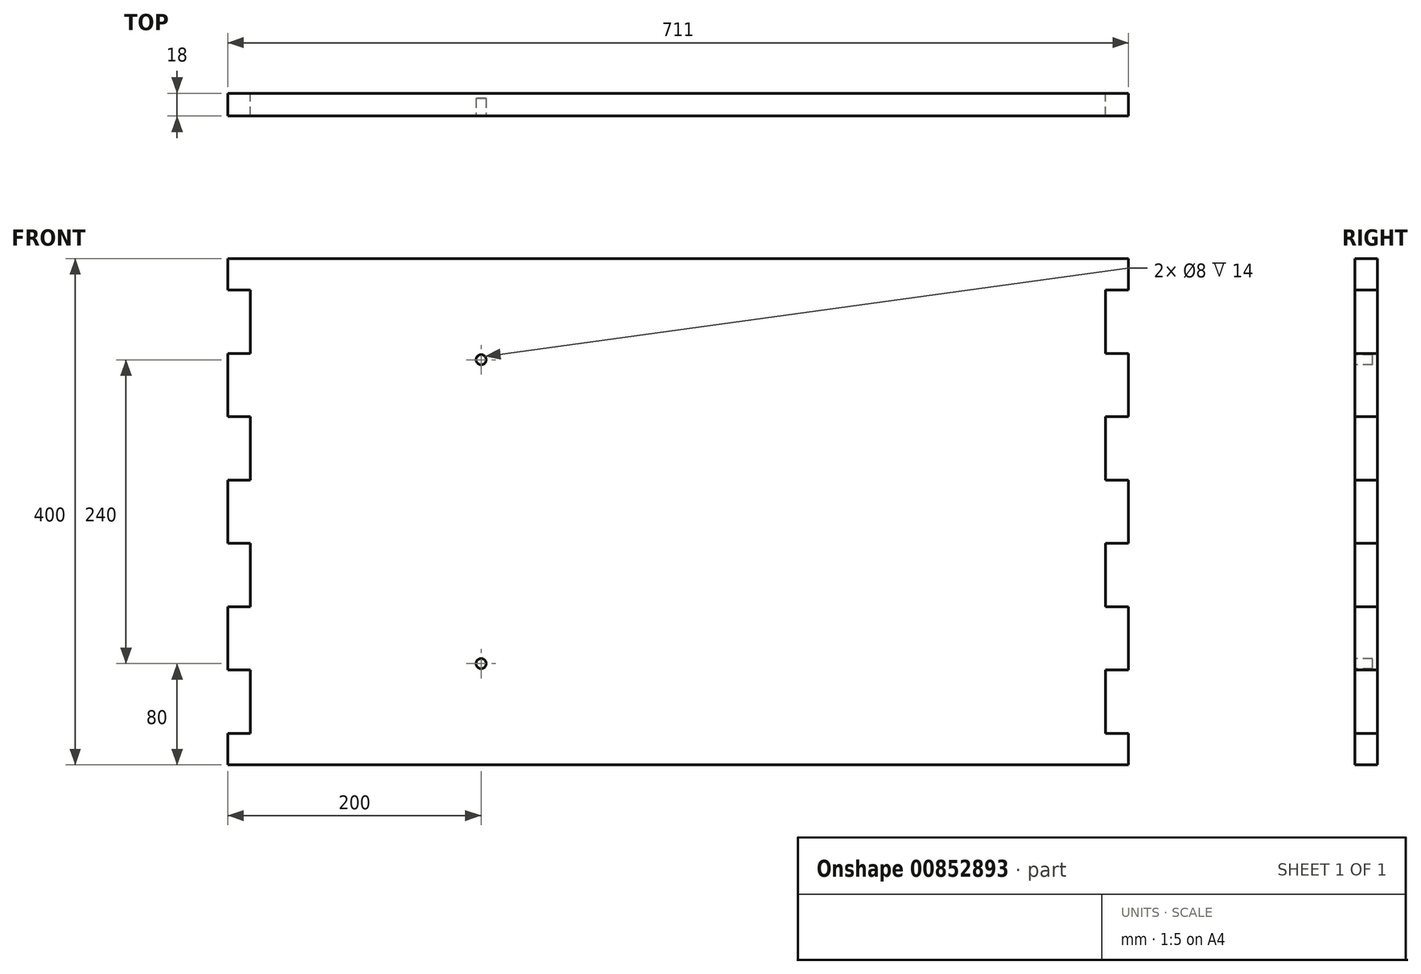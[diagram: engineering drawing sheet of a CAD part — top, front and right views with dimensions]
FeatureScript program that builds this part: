
annotation { "Feature Type Name" : "Feature", "Feature Type Description" : "" }
export const myFeature = defineFeature(function(context is Context, id is Id, definition is map)
    precondition{}
    {
        {
            var Q0;
            Q0=qCreatedBy(makeId("Front.planeOp"),FACE);
            var sketch = newSketch(context, id + "F0", { "sketchPlane" : qUnion([Q0])});
            skPoint(sketch, "E0.middle", {"position": v(0, 0) * mm});
            skLineSegment(sketch, "E1", {"start": v(-355.5, 202) * mm, "end": v(355.5, 202) * mm});
            skLineSegment(sketch, "E2", {"start": v(-355.5, -198) * mm, "end": v(355.5, -198) * mm});
            skLineSegment(sketch, "E3", {"start": v(355.5, 202) * mm, "end": v(355.5, 177) * mm});
            skLineSegment(sketch, "E4", {"start": v(355.5, 177) * mm, "end": v(337.5, 177) * mm});
            skLineSegment(sketch, "E5", {"start": v(337.5, 177) * mm, "end": v(337.5, 127) * mm});
            skLineSegment(sketch, "E6", {"start": v(337.5, 127) * mm, "end": v(355.5, 127) * mm});
            skLineSegment(sketch, "E7", {"start": v(355.5, 127) * mm, "end": v(355.5, 77) * mm});
            skLineSegment(sketch, "E8", {"start": v(355.5, 77) * mm, "end": v(337.5, 77) * mm});
            skLineSegment(sketch, "E9", {"start": v(337.5, 77) * mm, "end": v(337.5, 27) * mm});
            skLineSegment(sketch, "E10", {"start": v(337.5, 27) * mm, "end": v(355.5, 27) * mm});
            skLineSegment(sketch, "E11", {"start": v(355.5, 27) * mm, "end": v(355.5, -23) * mm});
            skLineSegment(sketch, "E12", {"start": v(355.5, -23) * mm, "end": v(337.5, -23) * mm});
            skLineSegment(sketch, "E13", {"start": v(337.5, -23) * mm, "end": v(337.5, -73) * mm});
            skLineSegment(sketch, "E14", {"start": v(337.5, -73) * mm, "end": v(355.5, -73) * mm});
            skLineSegment(sketch, "E15", {"start": v(355.5, -73) * mm, "end": v(355.5, -123) * mm});
            skLineSegment(sketch, "E16", {"start": v(355.5, -123) * mm, "end": v(337.5, -123) * mm});
            skLineSegment(sketch, "E17", {"start": v(337.5, -123) * mm, "end": v(337.5, -173) * mm});
            skLineSegment(sketch, "E18", {"start": v(337.5, -173) * mm, "end": v(355.5, -173) * mm});
            skLineSegment(sketch, "E19", {"start": v(355.5, -173) * mm, "end": v(355.5, -198) * mm});
            skLineSegment(sketch, "E20.MirrorCS", {"start": v(-337.5, 177) * mm, "end": v(-337.5, 127) * mm});
            skLineSegment(sketch, "E21.MirrorCS", {"start": v(-337.5, 127) * mm, "end": v(-355.5, 127) * mm});
            skLineSegment(sketch, "E22.MirrorCS", {"start": v(-355.5, 77) * mm, "end": v(-337.5, 77) * mm});
            skLineSegment(sketch, "E23.MirrorCS", {"start": v(-337.5, 27) * mm, "end": v(-355.5, 27) * mm});
            skLineSegment(sketch, "E24.MirrorCS", {"start": v(-355.5, 127) * mm, "end": v(-355.5, 77) * mm});
            skLineSegment(sketch, "E25.MirrorCS", {"start": v(-337.5, 77) * mm, "end": v(-337.5, 27) * mm});
            skLineSegment(sketch, "E26.MirrorCS", {"start": v(-355.5, -123) * mm, "end": v(-337.5, -123) * mm});
            skLineSegment(sketch, "E27.MirrorCS", {"start": v(-337.5, -173) * mm, "end": v(-355.5, -173) * mm});
            skLineSegment(sketch, "E28.MirrorCS", {"start": v(-355.5, -73) * mm, "end": v(-355.5, -123) * mm});
            skLineSegment(sketch, "E29.MirrorCS", {"start": v(-337.5, -123) * mm, "end": v(-337.5, -173) * mm});
            skLineSegment(sketch, "E30.MirrorCS", {"start": v(-355.5, 27) * mm, "end": v(-355.5, -23) * mm});
            skLineSegment(sketch, "E31.MirrorCS", {"start": v(-337.5, -73) * mm, "end": v(-355.5, -73) * mm});
            skLineSegment(sketch, "E32.MirrorCS", {"start": v(-355.5, 177) * mm, "end": v(-337.5, 177) * mm});
            skLineSegment(sketch, "E33.MirrorCS", {"start": v(-337.5, -23) * mm, "end": v(-337.5, -73) * mm});
            skLineSegment(sketch, "E34.MirrorCS", {"start": v(-355.5, -23) * mm, "end": v(-337.5, -23) * mm});
            skLineSegment(sketch, "E35", {"start": v(-355.5, 202) * mm, "end": v(-355.5, 177) * mm});
            skLineSegment(sketch, "E36", {"start": v(-355.5, -173) * mm, "end": v(-355.5, -198) * mm});
            skSolve(sketch);
        }
        {
            var Q0;
            Q0=makeQuery(id+"F0.imprint","IMPRINT",FACE,{"disambiguationData":[TD([[makeQuery(id+"F0.imprint","IMPRINT",EDGE,{"derivedFrom":sQuery(id+"F0.wireOp",EDGE,"E1")}),-1.0]])]});
            extrude(context, id + "F1", {"entities" : qUnion([Q0]), "depth" : 18 * mm, "offsetDistance" : 25 * mm});
        }
        {
            var Q0;
            Q0=makeQuery(id+"F1.opExtrude","CAP_FACE",FACE,{"disambiguationData":[OSD([sQuery(id+"F0.wireOp",EDGE,"E1"),sQuery(id+"F0.wireOp",EDGE,"E2"),sQuery(id+"F0.wireOp",EDGE,"E3"),sQuery(id+"F0.wireOp",EDGE,"E4"),sQuery(id+"F0.wireOp",EDGE,"E5"),sQuery(id+"F0.wireOp",EDGE,"E6"),sQuery(id+"F0.wireOp",EDGE,"E7"),sQuery(id+"F0.wireOp",EDGE,"E8"),sQuery(id+"F0.wireOp",EDGE,"E9"),sQuery(id+"F0.wireOp",EDGE,"E10"),sQuery(id+"F0.wireOp",EDGE,"E11"),sQuery(id+"F0.wireOp",EDGE,"E12"),sQuery(id+"F0.wireOp",EDGE,"E13"),sQuery(id+"F0.wireOp",EDGE,"E14"),sQuery(id+"F0.wireOp",EDGE,"E15"),sQuery(id+"F0.wireOp",EDGE,"E16"),sQuery(id+"F0.wireOp",EDGE,"E17"),sQuery(id+"F0.wireOp",EDGE,"E18"),sQuery(id+"F0.wireOp",EDGE,"E19"),sQuery(id+"F0.wireOp",EDGE,"E20.MirrorCS"),sQuery(id+"F0.wireOp",EDGE,"E21.MirrorCS"),sQuery(id+"F0.wireOp",EDGE,"E22.MirrorCS"),sQuery(id+"F0.wireOp",EDGE,"E23.MirrorCS"),sQuery(id+"F0.wireOp",EDGE,"E24.MirrorCS"),sQuery(id+"F0.wireOp",EDGE,"E25.MirrorCS"),sQuery(id+"F0.wireOp",EDGE,"E26.MirrorCS"),sQuery(id+"F0.wireOp",EDGE,"E27.MirrorCS"),sQuery(id+"F0.wireOp",EDGE,"E28.MirrorCS"),sQuery(id+"F0.wireOp",EDGE,"E29.MirrorCS"),sQuery(id+"F0.wireOp",EDGE,"E30.MirrorCS"),sQuery(id+"F0.wireOp",EDGE,"E31.MirrorCS"),sQuery(id+"F0.wireOp",EDGE,"E32.MirrorCS"),sQuery(id+"F0.wireOp",EDGE,"E33.MirrorCS"),sQuery(id+"F0.wireOp",EDGE,"E34.MirrorCS"),sQuery(id+"F0.wireOp",EDGE,"E35"),sQuery(id+"F0.wireOp",EDGE,"E36")])],"isStart":false});
            var sketch = newSketch(context, id + "F2", { "sketchPlane" : qUnion([Q0])});
            skCircle(sketch, "E37", {"center": v(-155.5, 122) * mm, "radius": 4 * mm});
            skCircle(sketch, "E38", {"center": v(-155.5, -118) * mm, "radius": 4 * mm});
            skSolve(sketch);
        }
        {
            var Q0;
            Q0=makeQuery(id+"F2.imprint","IMPRINT",FACE,{"disambiguationData":[TD([[makeQuery(id+"F2.imprint","IMPRINT",EDGE,{"derivedFrom":sQuery(id+"F2.wireOp",EDGE,"E38")}),1.0]])]});
            var Q1;
            Q1=makeQuery(id+"F2.imprint","IMPRINT",FACE,{"disambiguationData":[TD([[makeQuery(id+"F2.imprint","IMPRINT",EDGE,{"derivedFrom":sQuery(id+"F2.wireOp",EDGE,"E37")}),1.0]])]});
            extrude(context, id + "F3", {"entities" : qUnion([Q0, Q1]), "operationType" : NewBodyOperationType.REMOVE, "oppositeDirection" : true, "depth" : 14 * mm, "offsetDistance" : 25 * mm});
        }
    });
